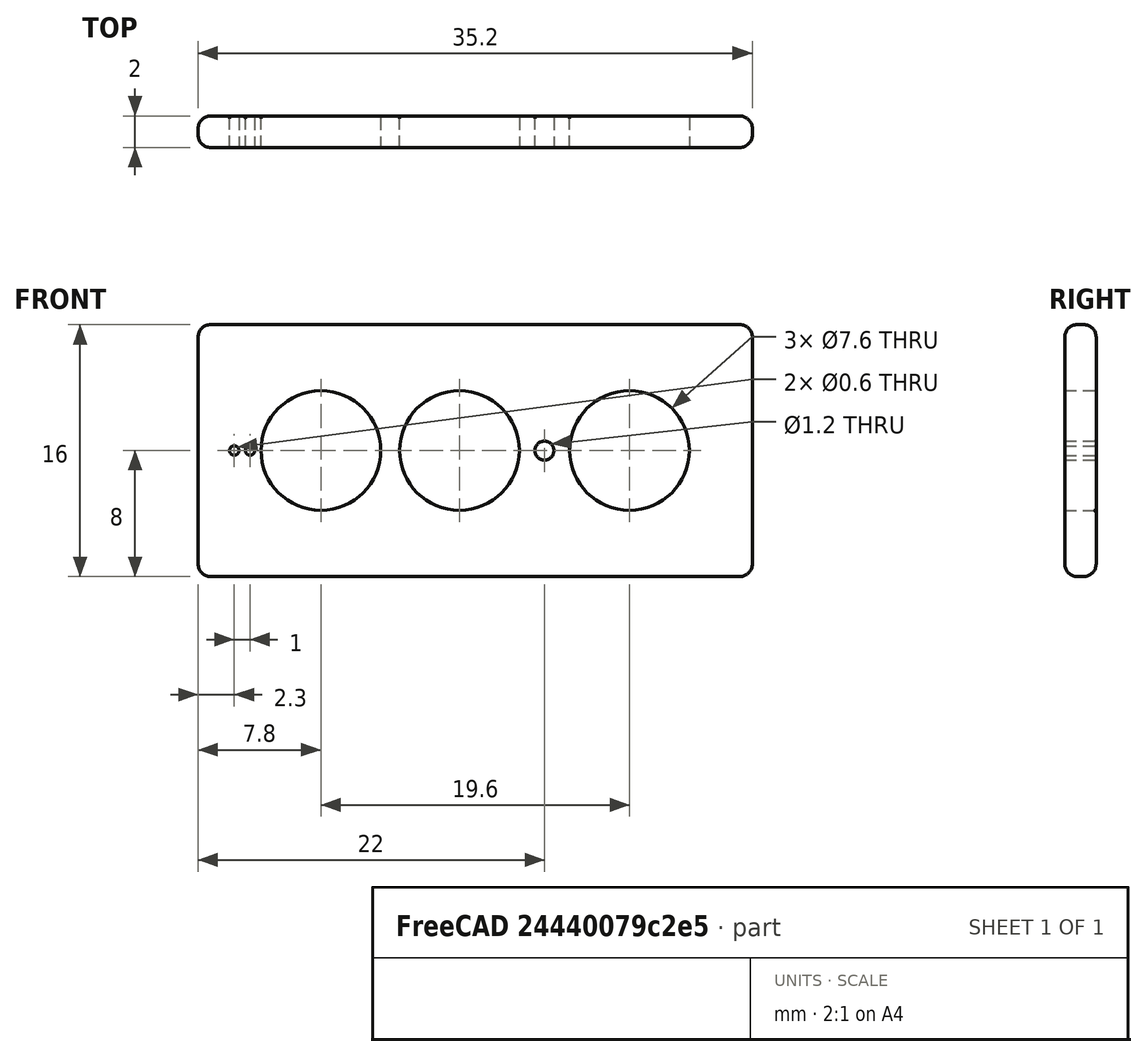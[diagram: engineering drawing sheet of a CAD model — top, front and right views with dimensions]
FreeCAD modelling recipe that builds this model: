
FCSTD DOCUMENT  (FreeCAD 0.16R6712 (Git))
Label: top3
License: All rights reserved
LicenseURL: http://en.wikipedia.org/wiki/All_rights_reserved
objects: Sketcher::SketchObject×2, PartDesign::Fillet×2, PartDesign::Pad×1, PartDesign::Pocket×1, Mesh::Feature×1
note: 8 computed .brp shape members not serialized (recipe doc carries the construction recipe); baked Part::Feature solids carry a one-line shape summary decoded from their .brp

FEATURE [Sketcher::SketchObject] Sketch001
  Placement = pos=(0,-3,0) rot=(1,0,0;1.5708rad)
  sketch-geometry (4):
    g0: LineSegment StartX=-17.6 StartY=8 StartZ=0 EndX=17.6 EndY=8 EndZ=0
    g1: LineSegment StartX=17.6 StartY=8 StartZ=0 EndX=17.6 EndY=-8 EndZ=0
    g2: LineSegment StartX=17.6 StartY=-8 StartZ=0 EndX=-17.6 EndY=-8 EndZ=0
    g3: LineSegment StartX=-17.6 StartY=-8 StartZ=0 EndX=-17.6 EndY=8 EndZ=0
  constraints (12):
    c: Coincident(g0,g1)
    c: Coincident(g1,g2)
    c: Coincident(g2,g3)
    c: Coincident(g3,g0)
    c: Horizontal(g0)
    c: Horizontal(g2)
    c: Vertical(g1)
    c: Vertical(g3)
    c: Symmetric(g0,g0,g-2)
    c: Symmetric(g1,g0,g-1)
    c: DistanceX(g-2,g0) = 17.6
    c: DistanceY(g-1,g0) = 8
FEATURE [PartDesign::Pad] Pad
  Length = 2
  Length2 = 100
  Placement = pos=(0,-3,0) rot=(1,0,0;1.5708rad)
  Sketch = -> Sketch001
  Type = 0
FEATURE [PartDesign::Fillet] Fillet
  Base = -> Pad [Edge4,Edge7,Edge10,Edge12,Edge5,Edge8,Edge9,Edge1,Edge11,Edge3,Edge6,Edge2]
  Placement = pos=(0,-3,0) rot=(1,0,0;1.5708rad)
  Radius = 0.8
FEATURE [Sketcher::SketchObject] Sketch002
  Placement = pos=(0,-3,0) rot=(-1,0,0;1.5708rad)
  Support = -> Fillet [Face13]
  sketch-geometry (6):
    g0: Circle CenterX=-1 CenterY=0 CenterZ=0 NormalX=0 NormalY=0 NormalZ=1 Radius=3.8
    g1: Circle CenterX=9.8 CenterY=0 CenterZ=0 NormalX=0 NormalY=0 NormalZ=1 Radius=3.8
    g2: Circle CenterX=-9.8 CenterY=0 CenterZ=0 NormalX=0 NormalY=0 NormalZ=1 Radius=3.8
    g3: Circle CenterX=4.4 CenterY=0 CenterZ=0 NormalX=0 NormalY=0 NormalZ=1 Radius=0.6
    g4: Circle CenterX=-14.3 CenterY=0 CenterZ=0 NormalX=0 NormalY=0 NormalZ=1 Radius=0.3
    g5: Circle CenterX=-15.3 CenterY=0 CenterZ=0 NormalX=0 NormalY=0 NormalZ=1 Radius=0.3
  constraints (17):
    c: Radius(g2) = 3.8
    c: Equal(g0,g1)
    c: PointOnObject(g1,g-1)
    c: PointOnObject(g0,g-1)
    c: PointOnObject(g2,g-1)
    c: DistanceX(g-2,g0) = -1
    c: DistanceX(g-2,g1) = 9.8
    c: Distance(g-1,g2) = 9.8
    c: PointOnObject(g3,g-1)
    c: Radius(g3) = 0.6
    c: Distance(g0,g3) = 5.4
    c: PointOnObject(g4,g-1)
    c: PointOnObject(g5,g-1)
    c: Radius(g5) = 0.3
    c: Equal(g4,g5)
    c: DistanceX(g4,g2) = 4.5
    c: DistanceX(g5,g4) = 1
FEATURE [PartDesign::Pocket] Pocket
  Length = 5
  Placement = pos=(0,-3,0) rot=(1,0,0;1.5708rad)
  Sketch = -> Sketch002
  Type = 0
FEATURE [PartDesign::Fillet] Fillet001
  Base = -> Pocket [Edge47,Edge44,Edge48,Edge43,Edge46,Edge45]
  Placement = pos=(0,-3,0) rot=(1,0,0;1.5708rad)
  Radius = 0.15
FEATURE [Mesh::Feature] Mesh  label="Fillet001 (Meshed)"
